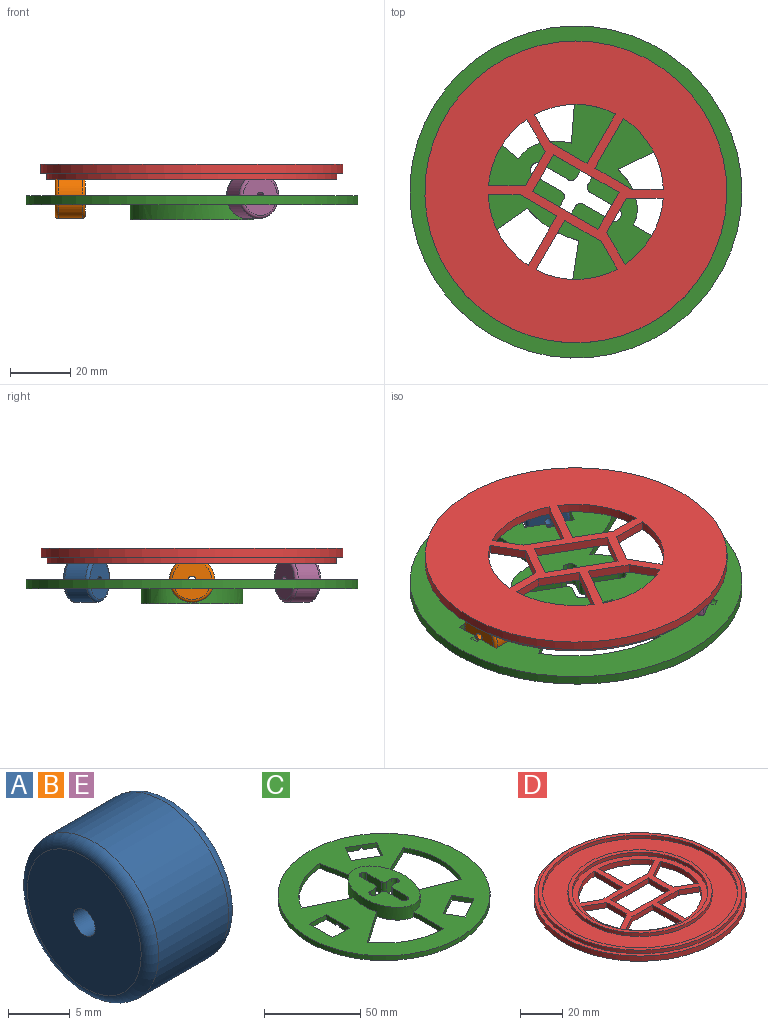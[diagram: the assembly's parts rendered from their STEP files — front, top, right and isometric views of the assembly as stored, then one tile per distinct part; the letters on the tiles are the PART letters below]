
ASSEMBLY  parts=5 mates=4
PART A: 6 faces, bbox 10x16.2x16.2 mm
  f0: cylinder r=1.25mm len=10mm, axis (-1,0,0), area 78.5mm2, adj f2,f3
  f1: cylinder r=7.5mm len=15mm, axis (-1,0,0), area 377mm2, adj f4,f5
  f2: plane 13x13mm, normal (1,0,0), area 127.8mm2, adj f0,f5
  f3: plane 13x13mm, normal (-1,0,0), area 127.8mm2, adj f0,f4
  f4: torus R=6.5mm, axis (1,0,0), area 70.4mm2, adj f1,f3
  f5: torus R=6.5mm, axis (1,0,0), area 70.4mm2, adj f1,f2
PART B: same geometry as A
PART C: 62 faces, bbox 110x110x8 mm
  f0: plane 110x110mm, normal (0,0,-1), area 6241.8mm2, adj f1,f2,f3,f4,f5,f6,f7,f8
  f1: plane 25.52x12.28mm, normal (0.43,0.9,0), area 85mm2, adj f0,f2,f23,f36
  f2: cylinder r=43.49mm len=35.08mm, axis (0,0,-1), area 128.9mm2, adj f0,f1,f3,f23
  f3: plane 21.41x3.71mm, normal (-0.99,-0.17,0), area 65.2mm2, adj f0,f2,f23,f36
  f4: plane 24.4x11.48mm, normal (0.43,-0.9,0), area 80.9mm2, adj f0,f5,f23,f36
  f5: cylinder r=43.49mm len=41.21mm, axis (0,0,-1), area 128.9mm2, adj f0,f4,f6,f23
  f6: plane 24.82x9.67mm, normal (0.36,0.93,0), area 79.9mm2, adj f0,f5,f23,f36
  f7: plane 21.58x3mm, normal (-1,0,0), area 64.7mm2, adj f0,f8,f23,f36
  f8: cylinder r=43.49mm len=36.3mm, axis (0,0,-1), area 128.9mm2, adj f0,f7,f18,f23
  f9: plane 17x3mm, normal (-1,0,0), area 48.3mm2, adj f0,f10,f19,f23,f53
  f10: plane 12x3mm, normal (0,1,0), area 36mm2, adj f0,f9,f11,f23
  f11: plane 17x3mm, normal (1,0,0), area 48.3mm2, adj f0,f10,f19,f23,f51
  f12: plane 10.39x6mm, normal (0.87,0.5,0), area 36mm2, adj f0,f13,f20,f23
  f13: plane 14.72x8.5mm, normal (0.5,-0.87,0), area 48.3mm2, adj f0,f12,f14,f23,f57
  f14: plane 10.39x6mm, normal (-0.87,-0.5,0), area 36mm2, adj f0,f13,f20,f23
  f15: plane 10.39x6mm, normal (-0.87,0.5,0), area 36mm2, adj f0,f16,f21,f23
  f16: plane 14.72x8.5mm, normal (0.5,0.87,0), area 48.3mm2, adj f0,f15,f17,f23,f61
  f17: plane 10.39x6mm, normal (0.87,-0.5,0), area 36mm2, adj f0,f16,f21,f23
  f18: plane 22.72x15.65mm, normal (0.57,-0.82,0), area 82.8mm2, adj f0,f8,f23,f36
  f19: plane 12x3mm, normal (0,-1,0), area 36mm2, adj f0,f9,f11,f23
  f20: plane 14.72x8.5mm, normal (-0.5,0.87,0), area 48.3mm2, adj f0,f12,f14,f23,f55
  f21: plane 14.72x8.5mm, normal (-0.5,-0.87,0), area 48.3mm2, adj f0,f15,f17,f23,f58
  f22: cylinder r=55mm len=110mm, axis (0,0,-1), area 1036.7mm2, adj f0,f23
  f23: plane 110x110mm, normal (0,0,1), area 5481.9mm2, adj f1,f2,f3,f4,f5,f6,f7,f8
  f24: plane 10.75x8mm, normal (1,0,0), area 86mm2, adj f0,f37,f38,f49
  f25: plane 8x0.5mm, normal (0,-1,0), area 4mm2, adj f0,f37,f38,f39
  f26: plane 10.75x8mm, normal (-1,0,0), area 86mm2, adj f0,f37,f39,f40
  f27: plane 8x3.75mm, normal (0,-1,0), area 30mm2, adj f0,f37,f40,f41
  f28: plane 8x0.5mm, normal (-1,0,0), area 4mm2, adj f0,f37,f41,f42
  f29: plane 8x3.75mm, normal (0,1,0), area 30mm2, adj f0,f37,f42,f43
  f30: plane 10.75x8mm, normal (-1,0,0), area 86mm2, adj f0,f37,f43,f44
  f31: plane 8x0.5mm, normal (0,1,0), area 4mm2, adj f0,f37,f44,f45
  f32: plane 10.75x8mm, normal (1,0,0), area 86mm2, adj f0,f37,f45,f46
  f33: plane 8x3.75mm, normal (0,1,0), area 30mm2, adj f0,f37,f46,f47
  f34: plane 8x0.5mm, normal (1,0,0), area 4mm2, adj f0,f37,f47,f48
  f35: plane 8x3.75mm, normal (0,-1,0), area 30mm2, adj f0,f37,f48,f49
  f36: extruded ~43.82x29.36mm, area 762mm2, adj f0,f1,f3,f4,f6,f7,f18,f23
  f37: plane 43.82x29.36mm, normal (0,0,1), area 791mm2, adj f24,f25,f26,f27,f28,f29,f30,f31
  f38: cylinder r=2mm len=8mm, axis (0,0,1), area 25.1mm2, adj f0,f24,f25,f37
  f39: cylinder r=2mm len=8mm, axis (0,0,-1), area 25.1mm2, adj f0,f25,f26,f37
  f40: cylinder r=2mm len=8mm, axis (0,0,1), area 25.1mm2, adj f0,f26,f27,f37
  f41: cylinder r=2mm len=8mm, axis (0,0,1), area 25.1mm2, adj f0,f27,f28,f37
  f42: cylinder r=2mm len=8mm, axis (0,0,-1), area 25.1mm2, adj f0,f28,f29,f37
  f43: cylinder r=2mm len=8mm, axis (0,0,1), area 25.1mm2, adj f0,f29,f30,f37
  f44: cylinder r=2mm len=8mm, axis (0,0,-1), area 25.1mm2, adj f0,f30,f31,f37
  f45: cylinder r=2mm len=8mm, axis (0,0,-1), area 25.1mm2, adj f0,f31,f32,f37
  f46: cylinder r=2mm len=8mm, axis (0,0,-1), area 25.1mm2, adj f0,f32,f33,f37
  f47: cylinder r=2mm len=8mm, axis (0,0,-1), area 25.1mm2, adj f0,f33,f34,f37
  f48: cylinder r=2mm len=8mm, axis (0,0,-1), area 25.1mm2, adj f0,f34,f35,f37
  f49: cylinder r=2mm len=8mm, axis (0,0,-1), area 25.1mm2, adj f0,f24,f35,f37
  f50: plane 2.6x1.3mm, normal (1,0,0), area 2.7mm2, adj f0,f51
  f51: cylinder r=1.3mm len=2.6mm, axis (1,0,0), area 8.2mm2, adj f0,f11,f50
  f52: plane 2.6x1.3mm, normal (-1,0,0), area 2.7mm2, adj f0,f53
  f53: cylinder r=1.3mm len=2.6mm, axis (1,0,0), area 8.2mm2, adj f0,f9,f52
  f54: plane 2.25x1.3mm, normal (-0.5,0.87,0), area 2.7mm2, adj f0,f55
  f55: cylinder r=1.3mm len=3.25mm, axis (0.5,-0.87,0), area 8.2mm2, adj f0,f20,f54
  f56: plane 2.25x1.3mm, normal (0.5,-0.87,0), area 2.7mm2, adj f0,f57
  f57: cylinder r=1.3mm len=3.25mm, axis (0.5,-0.87,0), area 8.2mm2, adj f0,f13,f56
  f58: cylinder r=1.3mm len=3.25mm, axis (0.5,0.87,0), area 8.2mm2, adj f0,f21,f59
  f59: plane 2.25x1.3mm, normal (-0.5,-0.87,0), area 2.7mm2, adj f0,f58
  f60: plane 2.25x1.3mm, normal (0.5,0.87,0), area 2.7mm2, adj f0,f61
  f61: cylinder r=1.3mm len=3.25mm, axis (0.5,0.87,0), area 8.2mm2, adj f0,f16,f60
PART D: 39 faces, bbox 100x100x5 mm
  f0: plane 92x92mm, normal (0,0,1), area 3015.9mm2, adj f34,f36
  f1: plane 64x64mm, normal (0,0,1), area 1095.9mm2, adj f2,f3,f4,f5,f6,f7,f8,f9
  f2: plane 14x3mm, normal (0,-1,0), area 42mm2, adj f1,f3,f30,f32
  f3: plane 9.16x5.26mm, normal (-0.5,-0.87,0), area 31.7mm2, adj f1,f2,f4,f32
  f4: cylinder r=29mm len=23.16mm, axis (0,0,-1), area 84mm2, adj f1,f3,f30,f32
  f5: plane 25x3mm, normal (0,1,0), area 75mm2, adj f1,f6,f23,f32
  f6: plane 14x3mm, normal (1,0,0), area 42mm2, adj f1,f5,f7,f32
  f7: plane 25x3mm, normal (0,-1,0), area 75mm2, adj f1,f6,f23,f32
  f8: cylinder r=29mm len=23.16mm, axis (0,0,-1), area 84mm2, adj f1,f9,f24,f32
  f9: plane 18.96x3mm, normal (-1,0,0), area 56.9mm2, adj f1,f8,f10,f32
  f10: plane 14x3mm, normal (0,1,0), area 42mm2, adj f1,f9,f24,f32
  f11: cylinder r=29mm len=23.16mm, axis (0,0,-1), area 84mm2, adj f1,f12,f25,f32
  f12: plane 9.16x5.26mm, normal (0.5,-0.87,0), area 31.7mm2, adj f1,f11,f13,f32
  f13: plane 14x3mm, normal (0,-1,0), area 42mm2, adj f1,f12,f25,f32
  f14: cylinder r=29mm len=25.26mm, axis (0,0,-1), area 78.4mm2, adj f1,f15,f26,f32
  f15: plane 10.61x6.09mm, normal (-0.5,-0.87,0), area 36.7mm2, adj f1,f14,f16,f32
  f16: plane 13.08x3mm, normal (-1,0,0), area 39.2mm2, adj f1,f15,f26,f32
  f17: cylinder r=29mm len=25.26mm, axis (0,0,-1), area 78.4mm2, adj f1,f18,f27,f32
  f18: plane 10.61x6.09mm, normal (0.5,0.87,0), area 36.7mm2, adj f1,f17,f19,f32
  f19: plane 13.08x3mm, normal (1,0,0), area 39.2mm2, adj f1,f18,f27,f32
  f20: plane 14x3mm, normal (0,1,0), area 42mm2, adj f1,f21,f28,f32
  f21: plane 18.96x3mm, normal (1,0,0), area 56.9mm2, adj f1,f20,f22,f32
  f22: cylinder r=29mm len=23.16mm, axis (0,0,-1), area 84mm2, adj f1,f21,f28,f32
  f23: plane 14x3mm, normal (-1,0,0), area 42mm2, adj f1,f5,f7,f32
  f24: plane 9.16x5.26mm, normal (0.5,0.87,0), area 31.7mm2, adj f1,f8,f10,f32
  f25: plane 18.96x3mm, normal (-1,0,0), area 56.9mm2, adj f1,f11,f13,f32
  f26: plane 10.61x6.09mm, normal (-0.5,0.87,0), area 36.7mm2, adj f1,f14,f16,f32
  f27: plane 10.61x6.09mm, normal (0.5,-0.87,0), area 36.7mm2, adj f1,f17,f19,f32
  f28: plane 9.16x5.26mm, normal (-0.5,0.87,0), area 31.7mm2, adj f1,f20,f22,f32
  f29: cylinder r=50mm len=100mm, axis (0,0,-1), area 942.5mm2, adj f31,f32
  f30: plane 18.96x3mm, normal (1,0,0), area 56.9mm2, adj f1,f2,f4,f32
  f31: plane 100x100mm, normal (0,0,1), area 615.8mm2, adj f29,f37
  f32: plane 100x100mm, normal (0,0,-1), area 5732.9mm2, adj f2,f3,f4,f5,f6,f7,f8,f9
  f33: cylinder r=32mm len=64mm, axis (0,0,-1), area 402.1mm2, adj f1,f35
  f34: cylinder r=34mm len=68mm, axis (0,0,-1), area 427.3mm2, adj f0,f35
  f35: plane 68x68mm, normal (0,0,1), area 414.7mm2, adj f33,f34
  f36: cylinder r=46mm len=92mm, axis (0,0,-1), area 578.1mm2, adj f0,f38
  f37: cylinder r=48mm len=96mm, axis (0,0,-1), area 603.2mm2, adj f31,f38
  f38: plane 96x96mm, normal (0,0,1), area 590.6mm2, adj f36,f37
PART E: same geometry as A
PLACE A rot(axis=(-0.77,-0.45,0.45),104.5deg) t=(198.19,-72.98,-36.41)mm
PLACE B rot(axis=(1,0,0),180deg) t=(135.24,-103.55,-36.41)mm
PLACE C rot(axis=(0.5,-0.87,0),180deg) t=(180.54,-103.55,-36.41)mm
PLACE D rot(axis=(0.97,-0.26,0),180deg) t=(180.54,-103.55,-25.91)mm
PLACE E rot(axis=(-0.5,-0.87,0),180deg) t=(203.19,-142.78,-36.41)mm
MATE revolute C.f55 <-> E.f0  axis (-0.5,0.87,0) through (203.54,-143.38,-36.41)mm
MATE revolute C.f58 <-> B.f0  axis (1,0,0) through (134.54,-103.55,-36.41)mm
MATE cylindrical D.f4 <-> C.f8  axis (0,0,-1) through (180.54,-103.55,-28.91)mm
MATE revolute C.f51 <-> A.f0  axis (-0.5,-0.87,0) through (203.54,-63.71,-36.41)mm
